# Revit family: ST115 REDUCING TEE
name_source: partatom
category: Pipe Fittings
units: mm (PartAtom-declared; Revit-internal decimal feet)

## family parameters
Always vertical = No
Cut with Voids When Loaded = No
Part Type = Tee
Round Connector Dimension = Use Diameter
Shared = No
Work Plane-Based = No

## types (98) — shared parameters
zero-valued in all types: Default Elevation

## type names (no varying parameters)
- 50X25
- 50X32
- 50X40
- 65X32
- 65X40
- 65X50
- 76.1X25
- 76.1X32
- 76.1X40
- 76.1X50
- 80X25
- 80X32
- 80X40
- 80X50
- 80X65
- 100X25
- 100X32
- 100X40
- 100X50
- 100X65
- 100X76.1
- 100X80
- 125X40
- 125X50
- 125X65
- 125X76.1
- 125X80
- 125X100
- 165.1X50
- 165.1X65
- 165.1X76.1
- 165.1X80
- 165.1X100
- 150X40
- 150X50
- 150X65
- 150X62
- 150X80
- 150X100
- 150X125
- 200X40
- 200X50
- 200X65
- 200X62
- 200X80
- 200X100
- 200X125
- 200X165.1
- 200X150
- 250X50
- 250X65
- 250X62
- 250X80
- 250X100
- 250X125
- 250X150
- 250X200
- 300X50
- 300X65
- 300X62
- 300X80
- 300X100
- 300X125
- 300X150
- 300X200
- 300X250
- 350X100
- 350X150
- 350X200
- 350X250
- 350X300
- 400X100
- 400X150
- 400X200
- 400X300
- 400X250
- 400X350
- 450X350
- 450X200
- 450X300
- 450X250
- 450X400
- 450X100
- 450X150
- 500x150
- 500x200
- 500x250
- 500x300
- 500x350
- 500x450
- 500x400
- 600x200
- 600x300
- 600x250
- 600x350
- 600x400
- 600x450
- 600x500

## geometry (parser evidence)
native form markers: Sweep x3
no freeform markers — native parametric forms only
